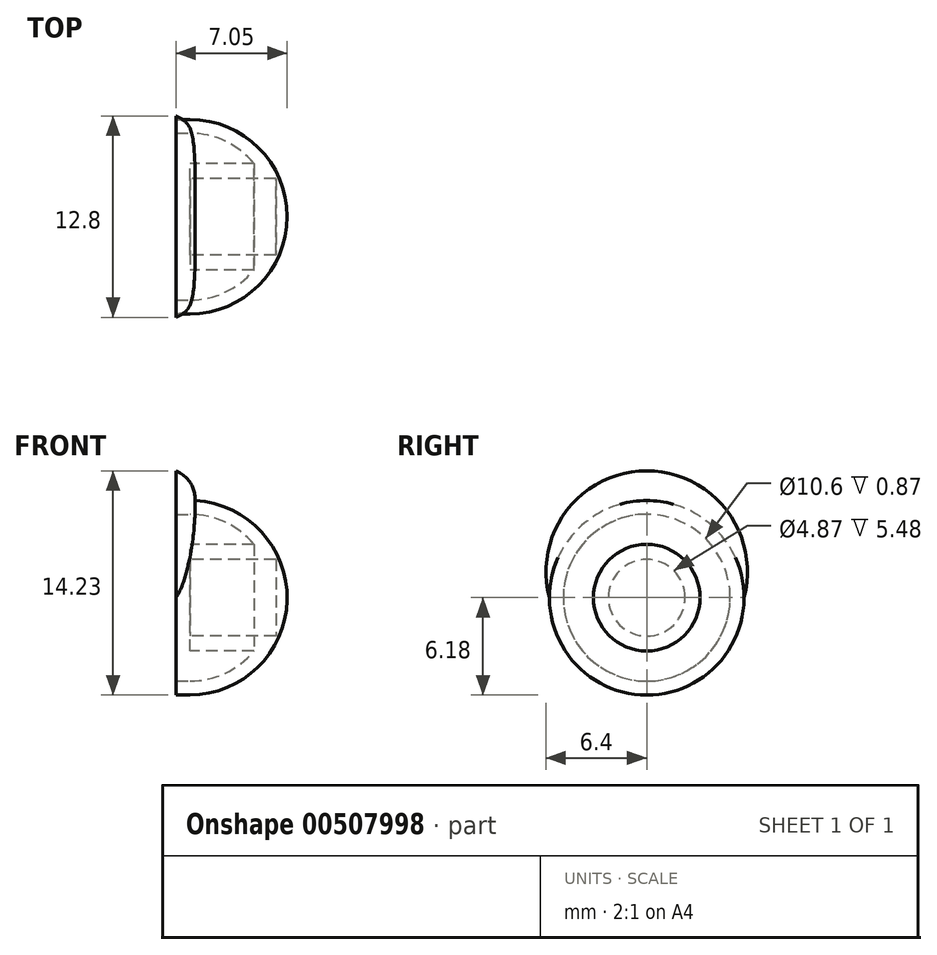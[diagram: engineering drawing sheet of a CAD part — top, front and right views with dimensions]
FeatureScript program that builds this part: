
annotation { "Feature Type Name" : "Feature", "Feature Type Description" : "" }
export const myFeature = defineFeature(function(context is Context, id is Id, definition is map)
    precondition{}
    {
        {
            var Q0;
            Q0=qCreatedBy(makeId("Front.planeOp"),FACE);
            var sketch = newSketch(context, id + "F0", { "sketchPlane" : qUnion([Q0])});
            skArc(sketch, "E0", {"start": v(0, -6.18) * mm, "mid": v(6.18, 0) * mm, "end": v(0, 6.18) * mm});
            skLineSegment(sketch, "E1", {"start": v(0, -6.18) * mm, "end": v(0, 6.18) * mm});
            skSolve(sketch);
        }
        {
            var Q0;
            Q0=makeQuery(id+"F0.imprint","IMPRINT",FACE,{"disambiguationData":[TD([[makeQuery(id+"F0.imprint","IMPRINT",EDGE,{"derivedFrom":sQuery(id+"F0.wireOp",EDGE,"E0")}),1.0]])]});
            var Q1;
            Q1=sQuery(id+"F0.wireOp",EDGE,"E1");
            revolve(context, id + "F1", {"entities" : qUnion([Q0]), "axis" : qUnion([Q1]), "revolveType" : RevolveType.SYMMETRIC, "angle" : 180 * degree});
        }
        {
            var Q0;
            Q0=makeQuery(id+"F1.opRevolve","CAP_FACE",FACE,{"disambiguationData":[OSD([sQuery(id+"F0.wireOp",EDGE,"E0"),sQuery(id+"F0.wireOp",EDGE,"E1")])],"isStart":true});
            extrude(context, id + "F2", {"entities" : qUnion([Q0]), "operationType" : NewBodyOperationType.ADD, "depth" : 0.87 * mm, "offsetDistance" : 25 * mm});
        }
        {
            var Q0;
            Q0=makeQuery(id+"F2.opExtrude","CAP_FACE",FACE,{"disambiguationData":[OSD([sQuery(id+"F0.wireOp",EDGE,"E0"),sQuery(id+"F0.wireOp",EDGE,"E1")])],"isStart":false});
            shell(context, id + "F3", {"entities" : qUnion([Q0]), "thickness" : 0.88 * mm});
        }
        {
            var Q0;
            Q0=qCreatedBy(makeId("Right.planeOp"),FACE);
            var sketch = newSketch(context, id + "F4", { "sketchPlane" : qUnion([Q0])});
            skCircle(sketch, "E2", {"center": v(0, 0) * mm, "radius": 3.4 * mm});
            skSolve(sketch);
        }
        {
            var Q0;
            Q0 = qSketchRegion(id + "F4", true);
            extrude(context, id + "F5", {"entities" : qUnion([Q0]), "operationType" : NewBodyOperationType.ADD, "depth" : 5.1 * mm, "offsetDistance" : 25 * mm});
        }
        {
            var Q0;
            Q0=makeQuery(id+"F5.opExtrude","CAP_FACE",FACE,{"disambiguationData":[OSD([sQuery(id+"F4.wireOp",EDGE,"E2")])],"isStart":true});
            var sketch = newSketch(context, id + "F6", { "sketchPlane" : qUnion([Q0])});
            skCircle(sketch, "E3", {"center": v(0, 0) * mm, "radius": 2.44 * mm});
            skSolve(sketch);
        }
        {
            var Q0;
            Q0 = qSketchRegion(id + "F6", true);
            extrude(context, id + "F7", {"entities" : qUnion([Q0]), "operationType" : NewBodyOperationType.REMOVE, "oppositeDirection" : true, "depth" : 5.48 * mm, "offsetDistance" : 25 * mm});
        }
        {
            var Q0;
            Q0=makeQuery(id+"F2.opExtrude","CAP_FACE",FACE,{"disambiguationData":[OSD([sQuery(id+"F0.wireOp",EDGE,"E0"),sQuery(id+"F0.wireOp",EDGE,"E1")])],"isStart":false});
            var sketch = newSketch(context, id + "F8", { "sketchPlane" : qUnion([Q0])});
            skArc(sketch, "E4", {"start": v(6.18, 0) * mm, "mid": v(0, 8.05) * mm, "end": v(-6.18, 0) * mm});
            skArc(sketch, "E5", {"start": v(6.18, 0) * mm, "mid": v(0, 5.77) * mm, "end": v(-6.18, 0) * mm});
            skSolve(sketch);
        }
        {
            var Q0;
            Q0 = qSketchRegion(id + "F8", true);
            extrude(context, id + "F9", {"entities" : qUnion([Q0]), "operationType" : NewBodyOperationType.ADD, "oppositeDirection" : true, "depth" : 1.21 * mm, "offsetDistance" : 25 * mm});
        }
        {
            var Q0;
            Q0=makeQuery(id+"F9.opExtrude","CAP_EDGE",EDGE,{"disambiguationData":[OSD([sQuery(id+"F8.wireOp",EDGE,"E4")])],"isStart":false});
            fillet(context, id + "F10", {"entities" : qUnion([Q0]), "radius" : 1.93 * mm, "tangentPropagation" : true, "allowEdgeOverflow" : false});
        }
    });
